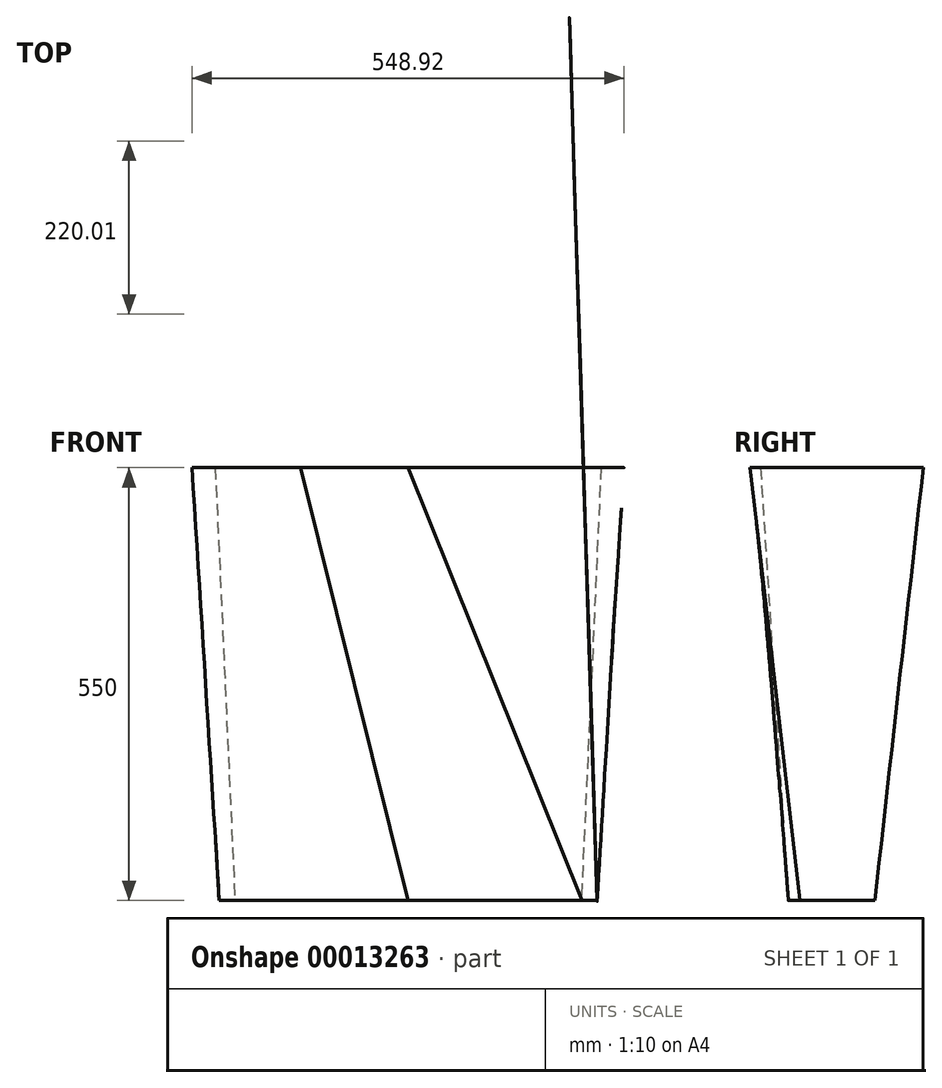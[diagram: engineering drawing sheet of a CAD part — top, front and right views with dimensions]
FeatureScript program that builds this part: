
annotation { "Feature Type Name" : "Feature", "Feature Type Description" : "" }
export const myFeature = defineFeature(function(context is Context, id is Id, definition is map)
    precondition{}
    {
        {
            var Q0;
            Q0=qCreatedBy(makeId("Top.planeOp"),FACE);
            var sketch = newSketch(context, id + "F0", { "sketchPlane" : qUnion([Q0])});
            skFitSpline(sketch, "E0.0", {"points": [v(245, 76.14) * mm, v(246.2, 76.14) * mm, v(247.38, 76.07) * mm, v(248.56, 75.92) * mm, v(249.74, 75.78) * mm, v(250.91, 75.56) * mm, v(252.07, 75.28) * mm, v(254.37, 74.7) * mm, v(256.57, 73.87) * mm, v(258.67, 72.76) * mm, v(259.7, 72.2) * mm, v(260.71, 71.6) * mm, v(261.68, 70.92) * mm, v(262.64, 70.25) * mm, v(263.56, 69.53) * mm, v(264.43, 68.76) * mm, v(265.3, 67.98) * mm, v(266.13, 67.15) * mm, v(266.9, 66.27) * mm, v(267.68, 65.4) * mm, v(268.4, 64.49) * mm, v(269.06, 63.53) * mm, v(269.72, 62.59) * mm, v(270.32, 61.6) * mm, v(270.86, 60.58) * mm, v(271.41, 59.56) * mm, v(271.9, 58.5) * mm, v(272.32, 57.43) * mm, v(272.74, 56.36) * mm, v(273.1, 55.27) * mm, v(273.4, 54.16) * mm, v(273.7, 53.06) * mm, v(273.94, 51.94) * mm, v(274.1, 50.8) * mm, v(274.28, 49.66) * mm, v(274.39, 48.52) * mm, v(274.43, 47.36) * mm, v(274.46, 46.79) * mm, v(274.46, 46.21) * mm, v(274.45, 45.64) * mm, v(274.45, 45.63) * mm, v(274.45, 45.34) * mm, v(274.44, 44.77) * mm, v(274.43, 44.49) * mm, v(274.43, 44.2) * mm, v(274.42, 43.91) * mm, v(274.38, 41.62) * mm, v(274.34, 39.32) * mm, v(274.3, 37.02) * mm, v(273.97, 18.84) * mm, v(273.65, 0.46) * mm, v(273.33, -18.13) * mm, v(273.17, -27.25) * mm, v(273, -36.44) * mm, v(272.85, -45.7) * mm, v(272.81, -48) * mm, v(272.77, -50.3) * mm, v(272.73, -52.6) * mm, v(272.71, -53.75) * mm, v(272.7, -54.9) * mm, v(272.67, -56.04) * mm, v(272.67, -56.46) * mm, v(272.66, -56.75) * mm, v(272.66, -56.9) * mm, v(272.65, -57.2) * mm, v(272.64, -57.48) * mm, v(272.63, -57.77) * mm, v(272.6, -58.34) * mm, v(272.58, -58.91) * mm, v(272.54, -59.49) * mm, v(272.38, -61.78) * mm, v(272.1, -64.06) * mm, v(271.67, -66.31) * mm, v(271.24, -68.6) * mm, v(270.68, -70.85) * mm, v(270, -73.07) * mm, v(269.3, -75.33) * mm, v(268.46, -77.53) * mm, v(267.5, -79.69) * mm, v(266.53, -81.84) * mm, v(265.44, -83.92) * mm, v(264.24, -85.93) * mm, v(263.03, -87.95) * mm, v(261.7, -89.9) * mm, v(260.23, -91.79) * mm, v(258.77, -93.68) * mm, v(257.2, -95.47) * mm, v(255.53, -97.16) * mm, v(253.86, -98.85) * mm, v(252.1, -100.44) * mm, v(250.23, -101.92) * mm, v(248.36, -103.4) * mm, v(246.4, -104.78) * mm, v(244.35, -106.04) * mm, v(242.3, -107.3) * mm, v(240.17, -108.44) * mm, v(237.98, -109.44) * mm, v(235.8, -110.45) * mm, v(233.56, -111.32) * mm, v(231.28, -112.05) * mm, v(230.12, -112.42) * mm, v(228.96, -112.75) * mm, v(227.79, -113.04) * mm, v(227.47, -113.12) * mm, v(227.13, -113.2) * mm, v(226.78, -113.29) * mm, v(226.44, -113.37) * mm, v(226.1, -113.45) * mm, v(225.76, -113.53) * mm, v(225.25, -113.64) * mm, v(224.74, -113.76) * mm, v(224.24, -113.88) * mm, v(221.87, -114.43) * mm, v(219.5, -114.97) * mm, v(217.11, -115.5) * mm, v(212.38, -116.57) * mm, v(207.62, -117.6) * mm, v(202.84, -118.6) * mm, v(193.37, -120.6) * mm, v(183.81, -122.48) * mm, v(174.17, -124.25) * mm, v(155.3, -127.7) * mm, v(136.04, -130.75) * mm, v(116.42, -133.37) * mm, v(106.83, -134.65) * mm, v(97.16, -135.83) * mm, v(87.41, -136.9) * mm, v(77.85, -137.96) * mm, v(68.16, -138.93) * mm, v(58.34, -139.8) * mm, v(48.73, -140.66) * mm, v(39.02, -141.43) * mm, v(29.2, -142.11) * mm, v(19.68, -142.77) * mm, v(9.95, -143.35) * mm, v(0, -143.86) * mm]});
            skFitSpline(sketch, "E0.1", {"points": [v(-245, 76.14) * mm, v(-163.33, 76.14) * mm, v(-81.66, 76.14) * mm, v(0, 76.14) * mm]});
            skFitSpline(sketch, "E0.2", {"points": [v(0, 76.14) * mm, v(81.67, 76.14) * mm, v(163.34, 76.14) * mm, v(245, 76.14) * mm]});
            skFitSpline(sketch, "E0.3", {"points": [v(0, -143.86) * mm, v(-9.83, -143.36) * mm, v(-19.45, -142.78) * mm, v(-28.87, -142.13) * mm, v(-38.57, -141.46) * mm, v(-48.18, -140.7) * mm, v(-57.68, -139.87) * mm, v(-67.4, -139) * mm, v(-76.98, -138.05) * mm, v(-86.44, -137.01) * mm, v(-96.09, -135.95) * mm, v(-105.65, -134.8) * mm, v(-115.14, -133.54) * mm, v(-134.55, -130.96) * mm, v(-153.6, -127.98) * mm, v(-172.26, -124.6) * mm, v(-181.8, -122.86) * mm, v(-191.25, -121.02) * mm, v(-200.62, -119.07) * mm, v(-205.35, -118.08) * mm, v(-210.06, -117.07) * mm, v(-214.74, -116.03) * mm, v(-217.09, -115.51) * mm, v(-219.43, -114.98) * mm, v(-221.78, -114.45) * mm, v(-222.95, -114.18) * mm, v(-224.12, -113.9) * mm, v(-225.3, -113.63) * mm, v(-226.23, -113.42) * mm, v(-226.82, -113.28) * mm, v(-227.05, -113.22) * mm, v(-227.64, -113.08) * mm, v(-228.22, -112.93) * mm, v(-228.8, -112.78) * mm, v(-231.12, -112.15) * mm, v(-233.4, -111.37) * mm, v(-235.65, -110.45) * mm, v(-237.86, -109.55) * mm, v(-240, -108.52) * mm, v(-242.1, -107.36) * mm, v(-244.17, -106.2) * mm, v(-246.17, -104.93) * mm, v(-248.09, -103.54) * mm, v(-250.02, -102.14) * mm, v(-251.86, -100.63) * mm, v(-253.62, -99) * mm, v(-255.35, -97.4) * mm, v(-256.98, -95.7) * mm, v(-258.5, -93.9) * mm, v(-260.03, -92.12) * mm, v(-261.44, -90.25) * mm, v(-262.74, -88.3) * mm, v(-264.04, -86.34) * mm, v(-265.23, -84.3) * mm, v(-266.3, -82.19) * mm, v(-267.35, -80.1) * mm, v(-268.28, -77.95) * mm, v(-269.08, -75.77) * mm, v(-269.87, -73.59) * mm, v(-270.54, -71.36) * mm, v(-271.08, -69.08) * mm, v(-271.62, -66.8) * mm, v(-272.02, -64.5) * mm, v(-272.29, -62.17) * mm, v(-272.42, -61.02) * mm, v(-272.52, -59.86) * mm, v(-272.58, -58.7) * mm, v(-272.61, -58.11) * mm, v(-272.64, -57.53) * mm, v(-272.65, -56.95) * mm, v(-272.66, -56.78) * mm, v(-272.66, -56.45) * mm, v(-272.67, -55.96) * mm, v(-272.68, -55.7) * mm, v(-272.68, -55.46) * mm, v(-272.68, -55.21) * mm, v(-272.72, -52.88) * mm, v(-272.76, -50.56) * mm, v(-272.8, -48.24) * mm, v(-272.96, -38.87) * mm, v(-273.12, -29.58) * mm, v(-273.28, -20.36) * mm, v(-273.61, -1.55) * mm, v(-273.94, 17.04) * mm, v(-274.26, 35.41) * mm, v(-274.3, 37.74) * mm, v(-274.35, 40.06) * mm, v(-274.39, 42.38) * mm, v(-274.43, 44.62) * mm, v(-274.45, 45.79) * mm, v(-274.45, 45.87) * mm, v(-274.46, 47.03) * mm, v(-274.4, 48.2) * mm, v(-274.29, 49.35) * mm, v(-274.17, 50.52) * mm, v(-273.98, 51.68) * mm, v(-273.73, 52.83) * mm, v(-273.47, 54) * mm, v(-273.14, 55.15) * mm, v(-272.75, 56.28) * mm, v(-272.35, 57.41) * mm, v(-271.9, 58.51) * mm, v(-271.37, 59.59) * mm, v(-270.84, 60.67) * mm, v(-270.25, 61.71) * mm, v(-269.6, 62.72) * mm, v(-268.94, 63.74) * mm, v(-268.23, 64.7) * mm, v(-267.45, 65.64) * mm, v(-266.67, 66.57) * mm, v(-265.84, 67.44) * mm, v(-264.97, 68.27) * mm, v(-264.08, 69.1) * mm, v(-263.14, 69.87) * mm, v(-262.15, 70.58) * mm, v(-261.16, 71.3) * mm, v(-260.13, 71.96) * mm, v(-259.05, 72.55) * mm, v(-257.98, 73.13) * mm, v(-256.88, 73.65) * mm, v(-255.74, 74.1) * mm, v(-254.6, 74.55) * mm, v(-253.43, 74.93) * mm, v(-252.23, 75.24) * mm, v(-251.04, 75.54) * mm, v(-249.84, 75.76) * mm, v(-248.62, 75.92) * mm, v(-247.42, 76.07) * mm, v(-246.2, 76.14) * mm, v(-245, 76.14) * mm]});
            skFitSpline(sketch, "E1", {"points": [v(245, 76.14) * mm, v(246.2, 76.14) * mm, v(247.38, 76.07) * mm, v(248.56, 75.92) * mm, v(249.74, 75.78) * mm, v(250.91, 75.56) * mm, v(252.07, 75.28) * mm, v(254.37, 74.7) * mm, v(256.57, 73.87) * mm, v(258.67, 72.76) * mm, v(259.7, 72.2) * mm, v(260.71, 71.6) * mm, v(261.68, 70.92) * mm, v(262.64, 70.25) * mm, v(263.56, 69.53) * mm, v(264.43, 68.76) * mm, v(265.3, 67.98) * mm, v(266.13, 67.15) * mm, v(266.9, 66.27) * mm, v(267.68, 65.4) * mm, v(268.4, 64.49) * mm, v(269.06, 63.53) * mm, v(269.72, 62.59) * mm, v(270.32, 61.6) * mm, v(270.86, 60.58) * mm, v(271.41, 59.56) * mm, v(271.9, 58.5) * mm, v(272.32, 57.43) * mm, v(272.74, 56.36) * mm, v(273.1, 55.27) * mm, v(273.4, 54.16) * mm, v(273.7, 53.06) * mm, v(273.94, 51.94) * mm, v(274.1, 50.8) * mm, v(274.28, 49.66) * mm, v(274.39, 48.52) * mm, v(274.43, 47.36) * mm, v(274.46, 46.79) * mm, v(274.46, 46.21) * mm, v(274.45, 45.64) * mm, v(274.45, 45.63) * mm, v(274.45, 45.34) * mm, v(274.44, 44.77) * mm, v(274.43, 44.49) * mm, v(274.43, 44.2) * mm, v(274.42, 43.91) * mm, v(274.38, 41.62) * mm, v(274.34, 39.32) * mm, v(274.3, 37.02) * mm, v(273.97, 18.84) * mm, v(273.65, 0.46) * mm, v(273.33, -18.13) * mm, v(273.17, -27.25) * mm, v(273, -36.44) * mm, v(272.85, -45.7) * mm, v(272.81, -48) * mm, v(272.77, -50.3) * mm, v(272.73, -52.6) * mm, v(272.71, -53.75) * mm, v(272.7, -54.9) * mm, v(272.67, -56.04) * mm, v(272.67, -56.46) * mm, v(272.66, -56.75) * mm, v(272.66, -56.9) * mm, v(272.65, -57.2) * mm, v(272.64, -57.48) * mm, v(272.63, -57.77) * mm, v(272.6, -58.34) * mm, v(272.58, -58.91) * mm, v(272.54, -59.49) * mm, v(272.38, -61.78) * mm, v(272.1, -64.06) * mm, v(271.67, -66.31) * mm, v(271.24, -68.6) * mm, v(270.68, -70.85) * mm, v(270, -73.07) * mm, v(269.3, -75.33) * mm, v(268.46, -77.53) * mm, v(267.5, -79.69) * mm, v(266.53, -81.84) * mm, v(265.44, -83.92) * mm, v(264.24, -85.93) * mm, v(263.03, -87.95) * mm, v(261.7, -89.9) * mm, v(260.23, -91.79) * mm, v(258.77, -93.68) * mm, v(257.2, -95.47) * mm, v(255.53, -97.16) * mm, v(253.86, -98.85) * mm, v(252.1, -100.44) * mm, v(250.23, -101.92) * mm, v(248.36, -103.4) * mm, v(246.4, -104.78) * mm, v(244.35, -106.04) * mm, v(242.3, -107.3) * mm, v(240.17, -108.44) * mm, v(237.98, -109.44) * mm, v(235.8, -110.45) * mm, v(233.56, -111.32) * mm, v(231.28, -112.05) * mm, v(230.12, -112.42) * mm, v(228.96, -112.75) * mm, v(227.79, -113.04) * mm, v(227.47, -113.12) * mm, v(227.13, -113.2) * mm, v(226.78, -113.29) * mm, v(226.44, -113.37) * mm, v(226.1, -113.45) * mm, v(225.76, -113.53) * mm, v(225.25, -113.64) * mm, v(224.74, -113.76) * mm, v(224.24, -113.88) * mm, v(221.87, -114.43) * mm, v(219.5, -114.97) * mm, v(217.11, -115.5) * mm, v(212.38, -116.57) * mm, v(207.62, -117.6) * mm, v(202.84, -118.6) * mm, v(193.37, -120.6) * mm, v(183.81, -122.48) * mm, v(174.17, -124.25) * mm, v(155.3, -127.7) * mm, v(136.04, -130.75) * mm, v(116.42, -133.37) * mm, v(106.83, -134.65) * mm, v(97.16, -135.83) * mm, v(87.41, -136.9) * mm, v(77.85, -137.96) * mm, v(68.16, -138.93) * mm, v(58.34, -139.8) * mm, v(48.73, -140.66) * mm, v(39.02, -141.43) * mm, v(29.2, -142.11) * mm, v(19.68, -142.77) * mm, v(9.95, -143.35) * mm, v(0, -143.86) * mm]});
            skFitSpline(sketch, "E2", {"points": [v(0, -143.86) * mm, v(-9.83, -143.36) * mm, v(-19.45, -142.78) * mm, v(-28.87, -142.13) * mm, v(-38.57, -141.46) * mm, v(-48.18, -140.7) * mm, v(-57.68, -139.87) * mm, v(-67.4, -139) * mm, v(-76.98, -138.05) * mm, v(-86.44, -137.01) * mm, v(-96.09, -135.95) * mm, v(-105.65, -134.8) * mm, v(-115.14, -133.54) * mm, v(-134.55, -130.96) * mm, v(-153.6, -127.98) * mm, v(-172.26, -124.6) * mm, v(-181.8, -122.86) * mm, v(-191.25, -121.02) * mm, v(-200.62, -119.07) * mm, v(-205.35, -118.08) * mm, v(-210.06, -117.07) * mm, v(-214.74, -116.03) * mm, v(-217.09, -115.51) * mm, v(-219.43, -114.98) * mm, v(-221.78, -114.45) * mm, v(-222.95, -114.18) * mm, v(-224.12, -113.9) * mm, v(-225.3, -113.63) * mm, v(-226.23, -113.42) * mm, v(-226.82, -113.28) * mm, v(-227.05, -113.22) * mm, v(-227.64, -113.08) * mm, v(-228.22, -112.93) * mm, v(-228.8, -112.78) * mm, v(-231.12, -112.15) * mm, v(-233.4, -111.37) * mm, v(-235.65, -110.45) * mm, v(-237.86, -109.55) * mm, v(-240, -108.52) * mm, v(-242.1, -107.36) * mm, v(-244.17, -106.2) * mm, v(-246.17, -104.93) * mm, v(-248.09, -103.54) * mm, v(-250.02, -102.14) * mm, v(-251.86, -100.63) * mm, v(-253.62, -99) * mm, v(-255.35, -97.4) * mm, v(-256.98, -95.7) * mm, v(-258.5, -93.9) * mm, v(-260.03, -92.12) * mm, v(-261.44, -90.25) * mm, v(-262.74, -88.3) * mm, v(-264.04, -86.34) * mm, v(-265.23, -84.3) * mm, v(-266.3, -82.19) * mm, v(-267.35, -80.1) * mm, v(-268.28, -77.95) * mm, v(-269.08, -75.77) * mm, v(-269.87, -73.59) * mm, v(-270.54, -71.36) * mm, v(-271.08, -69.08) * mm, v(-271.62, -66.8) * mm, v(-272.02, -64.5) * mm, v(-272.29, -62.17) * mm, v(-272.42, -61.02) * mm, v(-272.52, -59.86) * mm, v(-272.58, -58.7) * mm, v(-272.61, -58.11) * mm, v(-272.64, -57.53) * mm, v(-272.65, -56.95) * mm, v(-272.66, -56.78) * mm, v(-272.66, -56.45) * mm, v(-272.67, -55.96) * mm, v(-272.68, -55.7) * mm, v(-272.68, -55.46) * mm, v(-272.68, -55.21) * mm, v(-272.72, -52.88) * mm, v(-272.76, -50.56) * mm, v(-272.8, -48.24) * mm, v(-272.96, -38.87) * mm, v(-273.12, -29.58) * mm, v(-273.28, -20.36) * mm, v(-273.61, -1.55) * mm, v(-273.94, 17.04) * mm, v(-274.26, 35.41) * mm, v(-274.3, 37.74) * mm, v(-274.35, 40.06) * mm, v(-274.39, 42.38) * mm, v(-274.43, 44.62) * mm, v(-274.45, 45.79) * mm, v(-274.45, 45.87) * mm, v(-274.46, 47.03) * mm, v(-274.4, 48.2) * mm, v(-274.29, 49.35) * mm, v(-274.17, 50.52) * mm, v(-273.98, 51.68) * mm, v(-273.73, 52.83) * mm, v(-273.47, 54) * mm, v(-273.14, 55.15) * mm, v(-272.75, 56.28) * mm, v(-272.35, 57.41) * mm, v(-271.9, 58.51) * mm, v(-271.37, 59.59) * mm, v(-270.84, 60.67) * mm, v(-270.25, 61.71) * mm, v(-269.6, 62.72) * mm, v(-268.94, 63.74) * mm, v(-268.23, 64.7) * mm, v(-267.45, 65.64) * mm, v(-266.67, 66.57) * mm, v(-265.84, 67.44) * mm, v(-264.97, 68.27) * mm, v(-264.08, 69.1) * mm, v(-263.14, 69.87) * mm, v(-262.15, 70.58) * mm, v(-261.16, 71.3) * mm, v(-260.13, 71.96) * mm, v(-259.05, 72.55) * mm, v(-257.98, 73.13) * mm, v(-256.88, 73.65) * mm, v(-255.74, 74.1) * mm, v(-254.6, 74.55) * mm, v(-253.43, 74.93) * mm, v(-252.23, 75.24) * mm, v(-251.04, 75.54) * mm, v(-249.84, 75.76) * mm, v(-248.62, 75.92) * mm, v(-247.42, 76.07) * mm, v(-246.2, 76.14) * mm, v(-245, 76.14) * mm]});
            skFitSpline(sketch, "E3", {"points": [v(0, -143.86) * mm, v(-9.83, -143.36) * mm, v(-19.45, -142.78) * mm, v(-28.87, -142.13) * mm, v(-38.57, -141.46) * mm, v(-48.18, -140.7) * mm, v(-57.68, -139.87) * mm, v(-67.4, -139) * mm, v(-76.98, -138.05) * mm, v(-86.44, -137.01) * mm, v(-96.09, -135.95) * mm, v(-105.65, -134.8) * mm, v(-115.14, -133.54) * mm, v(-134.55, -130.96) * mm, v(-153.6, -127.98) * mm, v(-172.26, -124.6) * mm, v(-181.8, -122.86) * mm, v(-191.25, -121.02) * mm, v(-200.62, -119.07) * mm, v(-205.35, -118.08) * mm, v(-210.06, -117.07) * mm, v(-214.74, -116.03) * mm, v(-217.09, -115.51) * mm, v(-219.43, -114.98) * mm, v(-221.78, -114.45) * mm, v(-222.95, -114.18) * mm, v(-224.12, -113.9) * mm, v(-225.3, -113.63) * mm, v(-226.23, -113.42) * mm, v(-226.82, -113.28) * mm, v(-227.05, -113.22) * mm, v(-227.64, -113.08) * mm, v(-228.22, -112.93) * mm, v(-228.8, -112.78) * mm, v(-231.12, -112.15) * mm, v(-233.4, -111.37) * mm, v(-235.65, -110.45) * mm, v(-237.86, -109.55) * mm, v(-240, -108.52) * mm, v(-242.1, -107.36) * mm, v(-244.17, -106.2) * mm, v(-246.17, -104.93) * mm, v(-248.09, -103.54) * mm, v(-250.02, -102.14) * mm, v(-251.86, -100.63) * mm, v(-253.62, -99) * mm, v(-255.35, -97.4) * mm, v(-256.98, -95.7) * mm, v(-258.5, -93.9) * mm, v(-260.03, -92.12) * mm, v(-261.44, -90.25) * mm, v(-262.74, -88.3) * mm, v(-264.04, -86.34) * mm, v(-265.23, -84.3) * mm, v(-266.3, -82.19) * mm, v(-267.35, -80.1) * mm, v(-268.28, -77.95) * mm, v(-269.08, -75.77) * mm, v(-269.87, -73.59) * mm, v(-270.54, -71.36) * mm, v(-271.08, -69.08) * mm, v(-271.62, -66.8) * mm, v(-272.02, -64.5) * mm, v(-272.29, -62.17) * mm, v(-272.42, -61.02) * mm, v(-272.52, -59.86) * mm, v(-272.58, -58.7) * mm, v(-272.61, -58.11) * mm, v(-272.64, -57.53) * mm, v(-272.65, -56.95) * mm, v(-272.66, -56.78) * mm, v(-272.66, -56.45) * mm, v(-272.67, -55.96) * mm, v(-272.68, -55.7) * mm, v(-272.68, -55.46) * mm, v(-272.68, -55.21) * mm, v(-272.72, -52.88) * mm, v(-272.76, -50.56) * mm, v(-272.8, -48.24) * mm, v(-272.96, -38.87) * mm, v(-273.12, -29.58) * mm, v(-273.28, -20.36) * mm, v(-273.61, -1.55) * mm, v(-273.94, 17.04) * mm, v(-274.26, 35.41) * mm, v(-274.3, 37.74) * mm, v(-274.35, 40.06) * mm, v(-274.39, 42.38) * mm, v(-274.43, 44.62) * mm, v(-274.45, 45.79) * mm, v(-274.45, 45.87) * mm, v(-274.46, 47.03) * mm, v(-274.4, 48.2) * mm, v(-274.29, 49.35) * mm, v(-274.17, 50.52) * mm, v(-273.98, 51.68) * mm, v(-273.73, 52.83) * mm, v(-273.47, 54) * mm, v(-273.14, 55.15) * mm, v(-272.75, 56.28) * mm, v(-272.35, 57.41) * mm, v(-271.9, 58.51) * mm, v(-271.37, 59.59) * mm, v(-270.84, 60.67) * mm, v(-270.25, 61.71) * mm, v(-269.6, 62.72) * mm, v(-268.94, 63.74) * mm, v(-268.23, 64.7) * mm, v(-267.45, 65.64) * mm, v(-266.67, 66.57) * mm, v(-265.84, 67.44) * mm, v(-264.97, 68.27) * mm, v(-264.08, 69.1) * mm, v(-263.14, 69.87) * mm, v(-262.15, 70.58) * mm, v(-261.16, 71.3) * mm, v(-260.13, 71.96) * mm, v(-259.05, 72.55) * mm, v(-257.98, 73.13) * mm, v(-256.88, 73.65) * mm, v(-255.74, 74.1) * mm, v(-254.6, 74.55) * mm, v(-253.43, 74.93) * mm, v(-252.23, 75.24) * mm, v(-251.04, 75.54) * mm, v(-249.84, 75.76) * mm, v(-248.62, 75.92) * mm, v(-247.42, 76.07) * mm, v(-246.2, 76.14) * mm, v(-245, 76.14) * mm]});
            skFitSpline(sketch, "E4", {"points": [v(0, -143.86) * mm, v(-9.83, -143.36) * mm, v(-19.45, -142.78) * mm, v(-28.87, -142.13) * mm, v(-38.57, -141.46) * mm, v(-48.18, -140.7) * mm, v(-57.68, -139.87) * mm, v(-67.4, -139) * mm, v(-76.98, -138.05) * mm, v(-86.44, -137.01) * mm, v(-96.09, -135.95) * mm, v(-105.65, -134.8) * mm, v(-115.14, -133.54) * mm, v(-134.55, -130.96) * mm, v(-153.6, -127.98) * mm, v(-172.26, -124.6) * mm, v(-181.8, -122.86) * mm, v(-191.25, -121.02) * mm, v(-200.62, -119.07) * mm, v(-205.35, -118.08) * mm, v(-210.06, -117.07) * mm, v(-214.74, -116.03) * mm, v(-217.09, -115.51) * mm, v(-219.43, -114.98) * mm, v(-221.78, -114.45) * mm, v(-222.95, -114.18) * mm, v(-224.12, -113.9) * mm, v(-225.3, -113.63) * mm, v(-226.23, -113.42) * mm, v(-226.82, -113.28) * mm, v(-227.05, -113.22) * mm, v(-227.64, -113.08) * mm, v(-228.22, -112.93) * mm, v(-228.8, -112.78) * mm, v(-231.12, -112.15) * mm, v(-233.4, -111.37) * mm, v(-235.65, -110.45) * mm, v(-237.86, -109.55) * mm, v(-240, -108.52) * mm, v(-242.1, -107.36) * mm, v(-244.17, -106.2) * mm, v(-246.17, -104.93) * mm, v(-248.09, -103.54) * mm, v(-250.02, -102.14) * mm, v(-251.86, -100.63) * mm, v(-253.62, -99) * mm, v(-255.35, -97.4) * mm, v(-256.98, -95.7) * mm, v(-258.5, -93.9) * mm, v(-260.03, -92.12) * mm, v(-261.44, -90.25) * mm, v(-262.74, -88.3) * mm, v(-264.04, -86.34) * mm, v(-265.23, -84.3) * mm, v(-266.3, -82.19) * mm, v(-267.35, -80.1) * mm, v(-268.28, -77.95) * mm, v(-269.08, -75.77) * mm, v(-269.87, -73.59) * mm, v(-270.54, -71.36) * mm, v(-271.08, -69.08) * mm, v(-271.62, -66.8) * mm, v(-272.02, -64.5) * mm, v(-272.29, -62.17) * mm, v(-272.42, -61.02) * mm, v(-272.52, -59.86) * mm, v(-272.58, -58.7) * mm, v(-272.61, -58.11) * mm, v(-272.64, -57.53) * mm, v(-272.65, -56.95) * mm, v(-272.66, -56.78) * mm, v(-272.66, -56.45) * mm, v(-272.67, -55.96) * mm, v(-272.68, -55.7) * mm, v(-272.68, -55.46) * mm, v(-272.68, -55.21) * mm, v(-272.72, -52.88) * mm, v(-272.76, -50.56) * mm, v(-272.8, -48.24) * mm, v(-272.96, -38.87) * mm, v(-273.12, -29.58) * mm, v(-273.28, -20.36) * mm, v(-273.61, -1.55) * mm, v(-273.94, 17.04) * mm, v(-274.26, 35.41) * mm, v(-274.3, 37.74) * mm, v(-274.35, 40.06) * mm, v(-274.39, 42.38) * mm, v(-274.43, 44.62) * mm, v(-274.45, 45.79) * mm, v(-274.45, 45.87) * mm, v(-274.46, 47.03) * mm, v(-274.4, 48.2) * mm, v(-274.29, 49.35) * mm, v(-274.17, 50.52) * mm, v(-273.98, 51.68) * mm, v(-273.73, 52.83) * mm, v(-273.47, 54) * mm, v(-273.14, 55.15) * mm, v(-272.75, 56.28) * mm, v(-272.35, 57.41) * mm, v(-271.9, 58.51) * mm, v(-271.37, 59.59) * mm, v(-270.84, 60.67) * mm, v(-270.25, 61.71) * mm, v(-269.6, 62.72) * mm, v(-268.94, 63.74) * mm, v(-268.23, 64.7) * mm, v(-267.45, 65.64) * mm, v(-266.67, 66.57) * mm, v(-265.84, 67.44) * mm, v(-264.97, 68.27) * mm, v(-264.08, 69.1) * mm, v(-263.14, 69.87) * mm, v(-262.15, 70.58) * mm, v(-261.16, 71.3) * mm, v(-260.13, 71.96) * mm, v(-259.05, 72.55) * mm, v(-257.98, 73.13) * mm, v(-256.88, 73.65) * mm, v(-255.74, 74.1) * mm, v(-254.6, 74.55) * mm, v(-253.43, 74.93) * mm, v(-252.23, 75.24) * mm, v(-251.04, 75.54) * mm, v(-249.84, 75.76) * mm, v(-248.62, 75.92) * mm, v(-247.42, 76.07) * mm, v(-246.2, 76.14) * mm, v(-245, 76.14) * mm]});
            skFitSpline(sketch, "E5", {"points": [v(245, 76.14) * mm, v(246.2, 76.14) * mm, v(247.38, 76.07) * mm, v(248.56, 75.92) * mm, v(249.74, 75.78) * mm, v(250.91, 75.56) * mm, v(252.07, 75.28) * mm, v(254.37, 74.7) * mm, v(256.57, 73.87) * mm, v(258.67, 72.76) * mm, v(259.7, 72.2) * mm, v(260.71, 71.6) * mm, v(261.68, 70.92) * mm, v(262.64, 70.25) * mm, v(263.56, 69.53) * mm, v(264.43, 68.76) * mm, v(265.3, 67.98) * mm, v(266.13, 67.15) * mm, v(266.9, 66.27) * mm, v(267.68, 65.4) * mm, v(268.4, 64.49) * mm, v(269.06, 63.53) * mm, v(269.72, 62.59) * mm, v(270.32, 61.6) * mm, v(270.86, 60.58) * mm, v(271.41, 59.56) * mm, v(271.9, 58.5) * mm, v(272.32, 57.43) * mm, v(272.74, 56.36) * mm, v(273.1, 55.27) * mm, v(273.4, 54.16) * mm, v(273.7, 53.06) * mm, v(273.94, 51.94) * mm, v(274.1, 50.8) * mm, v(274.28, 49.66) * mm, v(274.39, 48.52) * mm, v(274.43, 47.36) * mm, v(274.46, 46.79) * mm, v(274.46, 46.21) * mm, v(274.45, 45.64) * mm, v(274.45, 45.63) * mm, v(274.45, 45.34) * mm, v(274.44, 44.77) * mm, v(274.43, 44.49) * mm, v(274.43, 44.2) * mm, v(274.42, 43.91) * mm, v(274.38, 41.62) * mm, v(274.34, 39.32) * mm, v(274.3, 37.02) * mm, v(273.97, 18.84) * mm, v(273.65, 0.46) * mm, v(273.33, -18.13) * mm, v(273.17, -27.25) * mm, v(273, -36.44) * mm, v(272.85, -45.7) * mm, v(272.81, -48) * mm, v(272.77, -50.3) * mm, v(272.73, -52.6) * mm, v(272.71, -53.75) * mm, v(272.7, -54.9) * mm, v(272.67, -56.04) * mm, v(272.67, -56.46) * mm, v(272.66, -56.75) * mm, v(272.66, -56.9) * mm, v(272.65, -57.2) * mm, v(272.64, -57.48) * mm, v(272.63, -57.77) * mm, v(272.6, -58.34) * mm, v(272.58, -58.91) * mm, v(272.54, -59.49) * mm, v(272.38, -61.78) * mm, v(272.1, -64.06) * mm, v(271.67, -66.31) * mm, v(271.24, -68.6) * mm, v(270.68, -70.85) * mm, v(270, -73.07) * mm, v(269.3, -75.33) * mm, v(268.46, -77.53) * mm, v(267.5, -79.69) * mm, v(266.53, -81.84) * mm, v(265.44, -83.92) * mm, v(264.24, -85.93) * mm, v(263.03, -87.95) * mm, v(261.7, -89.9) * mm, v(260.23, -91.79) * mm, v(258.77, -93.68) * mm, v(257.2, -95.47) * mm, v(255.53, -97.16) * mm, v(253.86, -98.85) * mm, v(252.1, -100.44) * mm, v(250.23, -101.92) * mm, v(248.36, -103.4) * mm, v(246.4, -104.78) * mm, v(244.35, -106.04) * mm, v(242.3, -107.3) * mm, v(240.17, -108.44) * mm, v(237.98, -109.44) * mm, v(235.8, -110.45) * mm, v(233.56, -111.32) * mm, v(231.28, -112.05) * mm, v(230.12, -112.42) * mm, v(228.96, -112.75) * mm, v(227.79, -113.04) * mm, v(227.47, -113.12) * mm, v(227.13, -113.2) * mm, v(226.78, -113.29) * mm, v(226.44, -113.37) * mm, v(226.1, -113.45) * mm, v(225.76, -113.53) * mm, v(225.25, -113.64) * mm, v(224.74, -113.76) * mm, v(224.24, -113.88) * mm, v(221.87, -114.43) * mm, v(219.5, -114.97) * mm, v(217.11, -115.5) * mm, v(212.38, -116.57) * mm, v(207.62, -117.6) * mm, v(202.84, -118.6) * mm, v(193.37, -120.6) * mm, v(183.81, -122.48) * mm, v(174.17, -124.25) * mm, v(155.3, -127.7) * mm, v(136.04, -130.75) * mm, v(116.42, -133.37) * mm, v(106.83, -134.65) * mm, v(97.16, -135.83) * mm, v(87.41, -136.9) * mm, v(77.85, -137.96) * mm, v(68.16, -138.93) * mm, v(58.34, -139.8) * mm, v(48.73, -140.66) * mm, v(39.02, -141.43) * mm, v(29.2, -142.11) * mm, v(19.68, -142.77) * mm, v(9.95, -143.35) * mm, v(0, -143.86) * mm]});
            skFitSpline(sketch, "E6", {"points": [v(245, 76.14) * mm, v(246.2, 76.14) * mm, v(247.38, 76.07) * mm, v(248.56, 75.92) * mm, v(249.74, 75.78) * mm, v(250.91, 75.56) * mm, v(252.07, 75.28) * mm, v(254.37, 74.7) * mm, v(256.57, 73.87) * mm, v(258.67, 72.76) * mm, v(259.7, 72.2) * mm, v(260.71, 71.6) * mm, v(261.68, 70.92) * mm, v(262.64, 70.25) * mm, v(263.56, 69.53) * mm, v(264.43, 68.76) * mm, v(265.3, 67.98) * mm, v(266.13, 67.15) * mm, v(266.9, 66.27) * mm, v(267.68, 65.4) * mm, v(268.4, 64.49) * mm, v(269.06, 63.53) * mm, v(269.72, 62.59) * mm, v(270.32, 61.6) * mm, v(270.86, 60.58) * mm, v(271.41, 59.56) * mm, v(271.9, 58.5) * mm, v(272.32, 57.43) * mm, v(272.74, 56.36) * mm, v(273.1, 55.27) * mm, v(273.4, 54.16) * mm, v(273.7, 53.06) * mm, v(273.94, 51.94) * mm, v(274.1, 50.8) * mm, v(274.28, 49.66) * mm, v(274.39, 48.52) * mm, v(274.43, 47.36) * mm, v(274.46, 46.79) * mm, v(274.46, 46.21) * mm, v(274.45, 45.64) * mm, v(274.45, 45.63) * mm, v(274.45, 45.34) * mm, v(274.44, 44.77) * mm, v(274.43, 44.49) * mm, v(274.43, 44.2) * mm, v(274.42, 43.91) * mm, v(274.38, 41.62) * mm, v(274.34, 39.32) * mm, v(274.3, 37.02) * mm, v(273.97, 18.84) * mm, v(273.65, 0.46) * mm, v(273.33, -18.13) * mm, v(273.17, -27.25) * mm, v(273, -36.44) * mm, v(272.85, -45.7) * mm, v(272.81, -48) * mm, v(272.77, -50.3) * mm, v(272.73, -52.6) * mm, v(272.71, -53.75) * mm, v(272.7, -54.9) * mm, v(272.67, -56.04) * mm, v(272.67, -56.46) * mm, v(272.66, -56.75) * mm, v(272.66, -56.9) * mm, v(272.65, -57.2) * mm, v(272.64, -57.48) * mm, v(272.63, -57.77) * mm, v(272.6, -58.34) * mm, v(272.58, -58.91) * mm, v(272.54, -59.49) * mm, v(272.38, -61.78) * mm, v(272.1, -64.06) * mm, v(271.67, -66.31) * mm, v(271.24, -68.6) * mm, v(270.68, -70.85) * mm, v(270, -73.07) * mm, v(269.3, -75.33) * mm, v(268.46, -77.53) * mm, v(267.5, -79.69) * mm, v(266.53, -81.84) * mm, v(265.44, -83.92) * mm, v(264.24, -85.93) * mm, v(263.03, -87.95) * mm, v(261.7, -89.9) * mm, v(260.23, -91.79) * mm, v(258.77, -93.68) * mm, v(257.2, -95.47) * mm, v(255.53, -97.16) * mm, v(253.86, -98.85) * mm, v(252.1, -100.44) * mm, v(250.23, -101.92) * mm, v(248.36, -103.4) * mm, v(246.4, -104.78) * mm, v(244.35, -106.04) * mm, v(242.3, -107.3) * mm, v(240.17, -108.44) * mm, v(237.98, -109.44) * mm, v(235.8, -110.45) * mm, v(233.56, -111.32) * mm, v(231.28, -112.05) * mm, v(230.12, -112.42) * mm, v(228.96, -112.75) * mm, v(227.79, -113.04) * mm, v(227.47, -113.12) * mm, v(227.13, -113.2) * mm, v(226.78, -113.29) * mm, v(226.44, -113.37) * mm, v(226.1, -113.45) * mm, v(225.76, -113.53) * mm, v(225.25, -113.64) * mm, v(224.74, -113.76) * mm, v(224.24, -113.88) * mm, v(221.87, -114.43) * mm, v(219.5, -114.97) * mm, v(217.11, -115.5) * mm, v(212.38, -116.57) * mm, v(207.62, -117.6) * mm, v(202.84, -118.6) * mm, v(193.37, -120.6) * mm, v(183.81, -122.48) * mm, v(174.17, -124.25) * mm, v(155.3, -127.7) * mm, v(136.04, -130.75) * mm, v(116.42, -133.37) * mm, v(106.83, -134.65) * mm, v(97.16, -135.83) * mm, v(87.41, -136.9) * mm, v(77.85, -137.96) * mm, v(68.16, -138.93) * mm, v(58.34, -139.8) * mm, v(48.73, -140.66) * mm, v(39.02, -141.43) * mm, v(29.2, -142.11) * mm, v(19.68, -142.77) * mm, v(9.95, -143.35) * mm, v(0, -143.86) * mm]});
            skSolve(sketch);
        }
        {
            var Q0;
            Q0=makeQuery(id+"F0.imprint","IMPRINT",FACE,{"disambiguationData":[TD([[makeQuery(id+"F0.imprint","IMPRINT",EDGE,{"derivedFrom":sQuery(id+"F0.wireOp",EDGE,"E0.0")}),-1.0]])]});
            cPlane(context, id + "F1", {"entities" : qUnion([Q0]), "cplaneType" : CPlaneType.OFFSET, "offset" : 550 * mm, "oppositeDirection" : true, "width" : 150 * mm, "height" : 150 * mm});
        }
        {
            var Q0;
            Q0=qCreatedBy(id+"F1.planeOp",FACE);
            var sketch = newSketch(context, id + "F2", { "sketchPlane" : qUnion([Q0])});
            skFitSpline(sketch, "E7.0", {"points": [v(221, -80.96) * mm, v(216.94, -81.97) * mm, v(212.73, -82.92) * mm, v(208.38, -83.8) * mm, v(204.21, -84.66) * mm, v(199.9, -85.47) * mm, v(195.44, -86.23) * mm, v(187.07, -87.65) * mm, v(178.19, -88.9) * mm, v(168.8, -89.96) * mm, v(160.13, -90.95) * mm, v(150.97, -91.8) * mm, v(141.33, -92.49) * mm, v(132.48, -93.13) * mm, v(123.13, -93.66) * mm, v(113.27, -94.07) * mm, v(104.4, -94.44) * mm, v(94.93, -94.73) * mm, v(84.86, -94.93) * mm, v(80.33, -95.02) * mm, v(75.57, -95.1) * mm, v(70.6, -95.15) * mm, v(66.14, -95.2) * mm, v(61.4, -95.25) * mm, v(56.36, -95.28) * mm, v(52.17, -95.3) * mm, v(47.43, -95.33) * mm, v(42.15, -95.34) * mm, v(39.24, -95.35) * mm, v(34.52, -95.36) * mm, v(28, -95.37) * mm, v(24.97, -95.38) * mm, v(22.63, -95.38) * mm, v(20.96, -95.39) * mm, v(18.37, -95.4) * mm, v(16.03, -95.4) * mm, v(13.94, -95.4) * mm, v(8.77, -95.43) * mm, v(4.13, -95.46) * mm, v(0, -95.5) * mm]});
            skFitSpline(sketch, "E7.1", {"points": [v(240, -56.69) * mm, v(240, -57.42) * mm, v(239.97, -58.14) * mm, v(239.9, -58.86) * mm, v(239.85, -59.54) * mm, v(239.76, -60.22) * mm, v(239.64, -60.9) * mm, v(239.42, -62.2) * mm, v(239.1, -63.46) * mm, v(238.68, -64.7) * mm, v(238.28, -65.88) * mm, v(237.8, -67.03) * mm, v(237.22, -68.15) * mm, v(236.65, -69.26) * mm, v(236, -70.31) * mm, v(235.27, -71.32) * mm, v(234.53, -72.35) * mm, v(233.71, -73.32) * mm, v(232.82, -74.22) * mm, v(231.88, -75.18) * mm, v(230.88, -76.05) * mm, v(229.8, -76.84) * mm, v(228.6, -77.71) * mm, v(227.35, -78.48) * mm, v(226.02, -79.13) * mm, v(225.28, -79.5) * mm, v(224.52, -79.82) * mm, v(223.73, -80.12) * mm, v(222.84, -80.45) * mm, v(221.93, -80.73) * mm, v(221, -80.96) * mm]});
            skFitSpline(sketch, "E7.2", {"points": [v(240, -5.5) * mm, v(240, -22.56) * mm, v(240, -39.63) * mm, v(240, -56.69) * mm]});
            skFitSpline(sketch, "E7.3", {"points": [v(220, 14.5) * mm, v(221.46, 14.5) * mm, v(222.91, 14.34) * mm, v(224.35, 14.02) * mm, v(225.04, 13.87) * mm, v(225.72, 13.68) * mm, v(226.4, 13.45) * mm, v(227.06, 13.23) * mm, v(227.7, 12.97) * mm, v(228.34, 12.68) * mm, v(229.58, 12.11) * mm, v(230.74, 11.42) * mm, v(231.84, 10.62) * mm, v(232.9, 9.83) * mm, v(233.89, 8.95) * mm, v(234.78, 7.98) * mm, v(235.64, 7.03) * mm, v(236.4, 6.01) * mm, v(237.07, 4.91) * mm, v(237.73, 3.85) * mm, v(238.27, 2.73) * mm, v(238.71, 1.56) * mm, v(239.14, 0.42) * mm, v(239.47, -0.75) * mm, v(239.68, -1.95) * mm, v(239.9, -3.13) * mm, v(240, -4.3) * mm, v(240, -5.5) * mm]});
            skFitSpline(sketch, "E7.4", {"points": [v(0, 14.5) * mm, v(73.33, 14.5) * mm, v(146.67, 14.5) * mm, v(220, 14.5) * mm]});
            skFitSpline(sketch, "E7.5", {"points": [v(-220, 14.5) * mm, v(-146.67, 14.5) * mm, v(-73.33, 14.5) * mm, v(0, 14.5) * mm]});
            skFitSpline(sketch, "E7.6", {"points": [v(0, -95.5) * mm, v(-4.13, -95.46) * mm, v(-8.77, -95.43) * mm, v(-13.94, -95.4) * mm, v(-16.03, -95.4) * mm, v(-18.37, -95.4) * mm, v(-20.96, -95.39) * mm, v(-22.63, -95.38) * mm, v(-24.97, -95.38) * mm, v(-28, -95.37) * mm, v(-34.52, -95.36) * mm, v(-39.23, -95.35) * mm, v(-42.15, -95.34) * mm, v(-47.43, -95.33) * mm, v(-52.17, -95.3) * mm, v(-56.36, -95.28) * mm, v(-61.4, -95.25) * mm, v(-66.14, -95.2) * mm, v(-70.6, -95.15) * mm, v(-75.57, -95.1) * mm, v(-80.32, -95.02) * mm, v(-84.86, -94.93) * mm, v(-94.93, -94.73) * mm, v(-104.4, -94.44) * mm, v(-113.27, -94.07) * mm, v(-123.13, -93.66) * mm, v(-132.48, -93.13) * mm, v(-141.33, -92.49) * mm, v(-150.97, -91.8) * mm, v(-160.13, -90.95) * mm, v(-168.8, -89.96) * mm, v(-178.18, -88.9) * mm, v(-187.07, -87.65) * mm, v(-195.44, -86.23) * mm, v(-199.9, -85.47) * mm, v(-204.21, -84.66) * mm, v(-208.38, -83.8) * mm, v(-212.73, -82.92) * mm, v(-216.94, -81.97) * mm, v(-221, -80.96) * mm]});
            skFitSpline(sketch, "E7.7", {"points": [v(-221, -80.96) * mm, v(-221.93, -80.73) * mm, v(-222.84, -80.45) * mm, v(-223.73, -80.12) * mm, v(-224.52, -79.82) * mm, v(-225.28, -79.5) * mm, v(-226.02, -79.13) * mm, v(-227.35, -78.48) * mm, v(-228.6, -77.71) * mm, v(-229.8, -76.84) * mm, v(-230.88, -76.05) * mm, v(-231.88, -75.18) * mm, v(-232.82, -74.22) * mm, v(-233.71, -73.32) * mm, v(-234.53, -72.35) * mm, v(-235.27, -71.32) * mm, v(-236, -70.32) * mm, v(-236.65, -69.26) * mm, v(-237.22, -68.15) * mm, v(-237.8, -67.03) * mm, v(-238.28, -65.88) * mm, v(-238.68, -64.7) * mm, v(-239.1, -63.46) * mm, v(-239.42, -62.2) * mm, v(-239.64, -60.9) * mm, v(-239.88, -59.51) * mm, v(-240, -58.1) * mm, v(-240, -56.69) * mm]});
            skFitSpline(sketch, "E7.8", {"points": [v(-240, -56.69) * mm, v(-240, -39.63) * mm, v(-240, -22.56) * mm, v(-240, -5.5) * mm]});
            skFitSpline(sketch, "E7.9", {"points": [v(-240, -5.5) * mm, v(-240, -4.31) * mm, v(-239.9, -3.13) * mm, v(-239.68, -1.95) * mm, v(-239.47, -0.75) * mm, v(-239.14, 0.42) * mm, v(-238.71, 1.56) * mm, v(-238.27, 2.73) * mm, v(-237.73, 3.85) * mm, v(-237.07, 4.91) * mm, v(-236.4, 6.01) * mm, v(-235.64, 7.03) * mm, v(-234.78, 7.98) * mm, v(-233.89, 8.95) * mm, v(-232.9, 9.83) * mm, v(-231.84, 10.62) * mm, v(-230.74, 11.42) * mm, v(-229.58, 12.11) * mm, v(-228.34, 12.68) * mm, v(-227.7, 12.97) * mm, v(-227.06, 13.23) * mm, v(-226.4, 13.45) * mm, v(-225.72, 13.68) * mm, v(-225.04, 13.87) * mm, v(-224.35, 14.02) * mm, v(-222.91, 14.34) * mm, v(-221.46, 14.5) * mm, v(-220, 14.5) * mm]});
            skSolve(sketch);
        }
        {
            var Q0;
            Q0=qCreatedBy(makeId("Right.planeOp"),FACE);
            var sketch = newSketch(context, id + "F3", { "sketchPlane" : qUnion([Q0])});
            skPoint(sketch, "E8.0", {"position": v(-143.86, 0) * mm});
            skPoint(sketch, "E9.0", {"position": v(-95.5, -550) * mm});
            skFitSpline(sketch, "E10", {"points": [v(-143.86, 0) * mm, v(-95.5, -550) * mm], "startDerivative": vector(25.48, -389.82) * mm, "endDerivative": vector(99.31, -276.13) * mm});
            skSolve(sketch);
        }
        {
            var Q0;
            Q0 = qSketchRegion(id + "F0", true);
            var Q1;
            Q1 = qSketchRegion(id + "F2", true);
            var Q2;
            Q2 = qConstructionFilter(qBodyType(qCreatedBy(id + "F3" ,EDGE), BodyType.WIRE), ConstructionObject.NO);
            loft(context, id + "F4", {"sheetProfilesArray" : [{ "sheetProfileEntities" : qUnion([Q0]) }, { "sheetProfileEntities" : qUnion([Q1]) }], "guidesArray" : [{ "guideEntities" : qUnion([Q2]), "guideDerivativeType" : LoftGuideDerivativeType.DEFAULT, "guideDerivativeMagnitude" : 1 }]});
        }
    });
